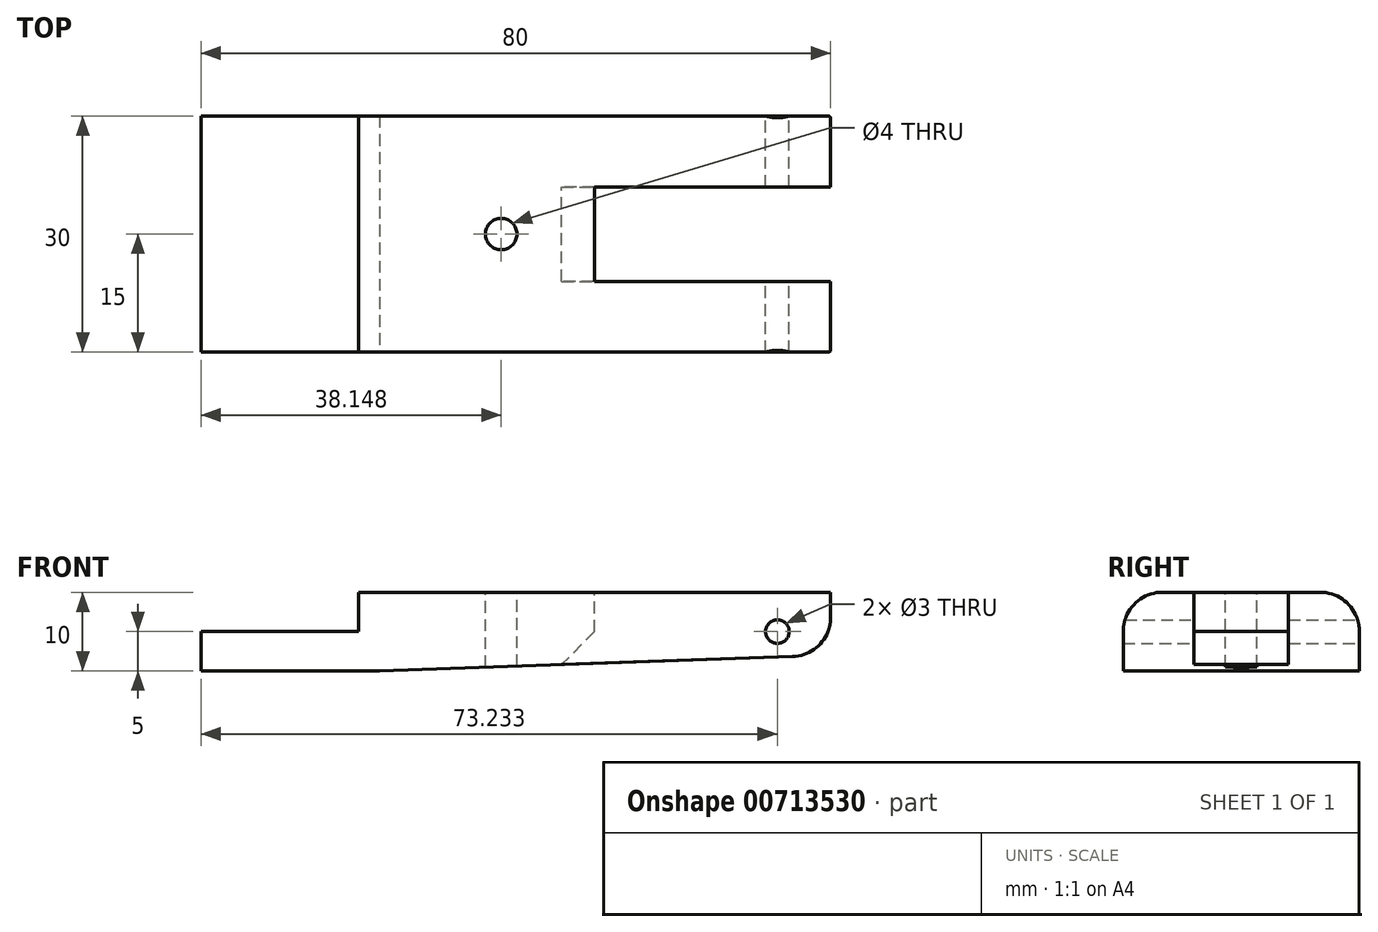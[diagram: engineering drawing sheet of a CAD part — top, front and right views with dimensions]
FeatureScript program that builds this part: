
annotation { "Feature Type Name" : "Feature", "Feature Type Description" : "" }
export const myFeature = defineFeature(function(context is Context, id is Id, definition is map)
    precondition{}
    {
        {
            var Q0;
            Q0=qCreatedBy(makeId("Front.planeOp"),FACE);
            var sketch = newSketch(context, id + "F0", { "sketchPlane" : qUnion([Q0])});
            skLineSegment(sketch, "E0.bottom", {"start": v(0, 0) * mm, "end": v(-80, 0) * mm});
            skLineSegment(sketch, "E0.top", {"start": v(0, 10) * mm, "end": v(-80, 10) * mm});
            skLineSegment(sketch, "E0.left", {"start": v(0, 0) * mm, "end": v(0, 10) * mm});
            skLineSegment(sketch, "E0.right", {"start": v(-80, 0) * mm, "end": v(-80, 10) * mm});
            skCircle(sketch, "E1", {"center": v(-6.77, 5) * mm, "radius": 1.5 * mm});
            skPoint(sketch, "E1.centerSnap0", {"position": v(0, 5) * mm});
            skSolve(sketch);
        }
        {
            var Q0;
            Q0=makeQuery(id+"F0.imprint","IMPRINT",FACE,{"disambiguationData":[TD([[makeQuery(id+"F0.imprint","IMPRINT",EDGE,{"derivedFrom":sQuery(id+"F0.wireOp",EDGE,"E0.bottom")}),-1.0]])]});
            extrude(context, id + "F1", {"entities" : qUnion([Q0]), "depth" : 30 * mm, "offsetDistance" : 25 * mm});
        }
        {
            var Q0;
            Q0=makeQuery(id+"F1.opExtrude","SWEPT_FACE",FACE,{"disambiguationData":[OSD([sQuery(id+"F0.wireOp",EDGE,"E0.top")])]});
            var sketch = newSketch(context, id + "F2", { "sketchPlane" : qUnion([Q0])});
            skLineSegment(sketch, "E2.bottom", {"start": v(0, -9) * mm, "end": v(-30, -9) * mm});
            skLineSegment(sketch, "E2.top", {"start": v(0, -21) * mm, "end": v(-30, -21) * mm});
            skLineSegment(sketch, "E2.left", {"start": v(0, -9) * mm, "end": v(0, -21) * mm});
            skLineSegment(sketch, "E2.right", {"start": v(-30, -9) * mm, "end": v(-30, -21) * mm});
            skPoint(sketch, "E2.middle", {"position": v(-15, -15) * mm});
            skPoint(sketch, "E2.middle.positionSnap0", {"position": v(0, -15) * mm});
            skPoint(sketch, "E2.centerSnap0", {"position": v(0, -15) * mm});
            skSolve(sketch);
        }
        {
            var Q0;
            Q0=makeQuery(id+"F2.imprint","IMPRINT",FACE,{"disambiguationData":[TD([[makeQuery(id+"F2.imprint","IMPRINT",EDGE,{"derivedFrom":sQuery(id+"F2.wireOp",EDGE,"E2.bottom")}),1.0]])]});
            extrude(context, id + "F3", {"entities" : qUnion([Q0]), "operationType" : NewBodyOperationType.REMOVE, "oppositeDirection" : true, "depth" : 25 * mm, "offsetDistance" : 25 * mm});
        }
        {
            var Q0;
            {var subQ0=sQuery(id+"F0.wireOp",EDGE,"E0.left");var subQ4=sQuery(id+"F0.wireOp",EDGE,"E0.top");Q0=makeQuery(id+"FIzBjTdNoyrMJFe_1.boolean.opBoolean","SPLIT",FACE,{"disambiguationData":[TD([makeQuery(id+"F1.opExtrude","SWEPT_FACE",FACE,{"disambiguationData":[OSD([subQ0])]})])],"derivedFrom":makeQuery(id+"F1.opExtrude","SWEPT_FACE",FACE,{"disambiguationData":[OSD([subQ4])]})});}
            var sketch = newSketch(context, id + "F4", { "sketchPlane" : qUnion([Q0])});
            skSolve(sketch);
        }
        {
            var Q0;
            {var subQ0=sQuery(id+"F0.wireOp",EDGE,"E0.left");var subQ4=sQuery(id+"F0.wireOp",EDGE,"E0.top");Q0=makeQuery(id+"FIzBjTdNoyrMJFe_1.boolean.opBoolean","SPLIT",FACE,{"disambiguationData":[TD([makeQuery(id+"F1.opExtrude","SWEPT_FACE",FACE,{"disambiguationData":[OSD([subQ0])]})])],"derivedFrom":makeQuery(id+"F1.opExtrude","SWEPT_FACE",FACE,{"disambiguationData":[OSD([subQ4])]})});}
            var sketch = newSketch(context, id + "F5", { "sketchPlane" : qUnion([Q0])});
            skCircle(sketch, "E3", {"center": v(-41.85, -15) * mm, "radius": 2 * mm});
            skPoint(sketch, "E3.centerSnap0", {"position": v(-42.07, -15) * mm});
            skPoint(sketch, "E4", {"position": v(-30, -15) * mm});
            skSolve(sketch);
        }
        {
            var Q0;
            Q0=makeQuery(id+"F5.imprint","IMPRINT",FACE,{"disambiguationData":[TD([[makeQuery(id+"F5.imprint","IMPRINT",EDGE,{"derivedFrom":sQuery(id+"F5.wireOp",EDGE,"E3")}),1.0]])]});
            extrude(context, id + "F6", {"entities" : qUnion([Q0]), "operationType" : NewBodyOperationType.REMOVE, "oppositeDirection" : true, "depth" : 25 * mm, "offsetDistance" : 25 * mm});
        }
        {
            var Q0;
            Q0=makeQuery(id+"F3.boolean.opBoolean","INTERSECT",EDGE,{"derivedFrom":[makeQuery(id+"F1.opExtrude","SWEPT_FACE",FACE,{"disambiguationData":[OSD([sQuery(id+"F0.wireOp",EDGE,"E0.bottom")])]}),makeQuery(id+"F3.opExtrude","SWEPT_FACE",FACE,{"disambiguationData":[OSD([sQuery(id+"F2.wireOp",EDGE,"E2.right")])]})]});
            chamfer(context, id + "F7", {"entities" : qUnion([Q0]), "width" : 5 * mm, "tangentPropagation" : true});
        }
        {
            var Q0;
            {var subQ1=sQuery(id+"F0.wireOp",EDGE,"E0.top");Q0=makeQuery(id+"F4.imprint","IMPRINT",FACE,{"disambiguationData":[TD([[makeQuery(id+"F4.imprint","IMPRINT",EDGE,{"derivedFrom":makeQuery(id+"F1.opExtrude","CAP_EDGE",EDGE,{"disambiguationData":[OSD([subQ1])],"isStart":true})}),1.0]])]});}
            var sketch = newSketch(context, id + "F8", { "sketchPlane" : qUnion([Q0])});
            skLineSegment(sketch, "E5.bottom", {"start": v(-80, 0) * mm, "end": v(-60, 0) * mm});
            skLineSegment(sketch, "E5.top", {"start": v(-80, -30) * mm, "end": v(-60, -30) * mm});
            skLineSegment(sketch, "E5.left", {"start": v(-80, 0) * mm, "end": v(-80, -30) * mm});
            skLineSegment(sketch, "E5.right", {"start": v(-60, 0) * mm, "end": v(-60, -30) * mm});
            skSolve(sketch);
        }
        {
            var Q0;
            Q0=makeQuery(id+"F8.imprint","IMPRINT",FACE,{"disambiguationData":[TD([[makeQuery(id+"F8.imprint","IMPRINT",EDGE,{"derivedFrom":sQuery(id+"F8.wireOp",EDGE,"E5.bottom")}),1.0]])]});
            extrude(context, id + "F9", {"entities" : qUnion([Q0]), "operationType" : NewBodyOperationType.REMOVE, "oppositeDirection" : true, "depth" : 5 * mm, "offsetDistance" : 25 * mm});
        }
        {
            var Q0;
            Q0=makeQuery(id+"F9.boolean.opBoolean","COPY",EDGE,{"derivedFrom":makeQuery(id+"F9.opExtrude","CAP_EDGE",EDGE,{"disambiguationData":[OSD([sQuery(id+"F8.wireOp",EDGE,"E5.left")])],"isStart":false})});
            var Q1;
            Q1=makeQuery(id+"F9.boolean.opBoolean","COPY",EDGE,{"derivedFrom":makeQuery(id+"F9.opExtrude","CAP_EDGE",EDGE,{"disambiguationData":[OSD([sQuery(id+"F8.wireOp",EDGE,"E5.top")])],"isStart":false})});
            var Q2;
            Q2=makeQuery(id+"F9.boolean.opBoolean","COPY",EDGE,{"derivedFrom":makeQuery(id+"F9.opExtrude","CAP_EDGE",EDGE,{"disambiguationData":[OSD([sQuery(id+"F8.wireOp",EDGE,"E5.bottom")])],"isStart":false})});
            var Q3;
            Q3=makeQuery(id+"F1.opExtrude","CAP_EDGE",EDGE,{"disambiguationData":[OSD([sQuery(id+"F0.wireOp",EDGE,"E0.top")])],"isStart":false});
            var Q4;
            Q4=makeQuery(id+"F1.opExtrude","CAP_EDGE",EDGE,{"disambiguationData":[OSD([sQuery(id+"F0.wireOp",EDGE,"E0.top")])],"isStart":true});
            var Q5;
            Q5=makeQuery(id+"F3.boolean.opBoolean","COPY",EDGE,{"derivedFrom":makeQuery(id+"F3.opExtrude","CAP_EDGE",EDGE,{"disambiguationData":[OSD([sQuery(id+"F2.wireOp",EDGE,"E2.bottom")])],"isStart":true})});
            var Q6;
            Q6=makeQuery(id+"F3.boolean.opBoolean","COPY",EDGE,{"derivedFrom":makeQuery(id+"F3.opExtrude","CAP_EDGE",EDGE,{"disambiguationData":[OSD([sQuery(id+"F2.wireOp",EDGE,"E2.top")])],"isStart":true})});
            var Q7;
            Q7=makeQuery(id+"F3.boolean.opBoolean","COPY",EDGE,{"derivedFrom":makeQuery(id+"F3.opExtrude","CAP_EDGE",EDGE,{"disambiguationData":[OSD([sQuery(id+"F2.wireOp",EDGE,"E2.right")])],"isStart":true})});
            fillet(context, id + "F10", {"entities" : qUnion([Q0, Q1, Q2, Q3, Q4, Q5, Q6, Q7]), "radius" : 5 * mm, "tangentPropagation" : true, "allowEdgeOverflow" : false});
        }
        {
            var Q0;
            {var subQ0=sQuery(id+"F0.wireOp",EDGE,"E0.bottom");var subQ1=sQuery(id+"F0.wireOp",EDGE,"E0.left");Q0=makeQuery(id+"F3.boolean.opBoolean","SPLIT",EDGE,{"disambiguationData":[TD([makeQuery(id+"F3.opExtrude","SWEPT_FACE",FACE,{"disambiguationData":[OSD([sQuery(id+"F2.wireOp",EDGE,"E2.bottom")])]})])],"derivedFrom":makeQuery(id+"F1.opExtrude","SWEPT_EDGE",EDGE,{"disambiguationData":[OSD([subQ0,subQ1])]})});}
            var Q1;
            {var subQ0=sQuery(id+"F0.wireOp",EDGE,"E0.bottom");var subQ1=sQuery(id+"F0.wireOp",EDGE,"E0.left");Q1=makeQuery(id+"F3.boolean.opBoolean","SPLIT",EDGE,{"disambiguationData":[TD([makeQuery(id+"F3.opExtrude","SWEPT_FACE",FACE,{"disambiguationData":[OSD([sQuery(id+"F2.wireOp",EDGE,"E2.top")])]})])],"derivedFrom":makeQuery(id+"F1.opExtrude","SWEPT_EDGE",EDGE,{"disambiguationData":[OSD([subQ0,subQ1])]})});}
            chamfer(context, id + "F11", {"entities" : qUnion([Q0, Q1]), "chamferType" : ChamferType.OFFSET_ANGLE, "width" : 2 * mm, "oppositeDirection" : false, "angle" : 88 * degree, "tangentPropagation" : true});
        }
        {
            var Q0;
            {var subQ0=sQuery(id+"F0.wireOp",EDGE,"E0.bottom");var subQ2=sQuery(id+"F0.wireOp",EDGE,"E0.left");var subQ5=makeQuery(id+"F3.opExtrude","SWEPT_FACE",FACE,{"disambiguationData":[OSD([sQuery(id+"F2.wireOp",EDGE,"E2.bottom")])]});var subQ6=makeQuery(id+"F1.opExtrude","SWEPT_FACE",FACE,{"disambiguationData":[OSD([subQ2])]});Q0=makeQuery(id+"F11.opChamfer","BLEND_EDGE",EDGE,{"blendedFrom":[makeQuery(id+"F3.boolean.opBoolean","SPLIT",EDGE,{"disambiguationData":[TD([subQ5])],"derivedFrom":makeQuery(id+"F1.opExtrude","SWEPT_EDGE",EDGE,{"disambiguationData":[OSD([subQ0,subQ2])]})}),makeQuery(id+"F3.boolean.opBoolean","SPLIT",FACE,{"disambiguationData":[TD([subQ5])],"derivedFrom":subQ6})],"blendedInto":[makeQuery(id+"F3.boolean.opBoolean","SPLIT",FACE,{"disambiguationData":[TD([subQ5])],"derivedFrom":subQ6})]});}
            var Q1;
            {var subQ0=sQuery(id+"F0.wireOp",EDGE,"E0.bottom");var subQ4=sQuery(id+"F0.wireOp",EDGE,"E0.left");var subQ6=makeQuery(id+"F1.opExtrude","SWEPT_FACE",FACE,{"disambiguationData":[OSD([subQ4])]});Q1=makeQuery(id+"F11.opChamfer","BLEND_EDGE",EDGE,{"blendedFrom":[makeQuery(id+"F3.boolean.opBoolean","SPLIT",EDGE,{"disambiguationData":[TD([makeQuery(id+"F3.opExtrude","SWEPT_FACE",FACE,{"disambiguationData":[OSD([sQuery(id+"F2.wireOp",EDGE,"E2.bottom")])]})])],"derivedFrom":makeQuery(id+"F1.opExtrude","SWEPT_EDGE",EDGE,{"disambiguationData":[OSD([subQ0,subQ4])]})}),makeQuery(id+"F3.boolean.opBoolean","SPLIT",FACE,{"disambiguationData":[TD([makeQuery(id+"F3.opExtrude","SWEPT_FACE",FACE,{"disambiguationData":[OSD([sQuery(id+"F2.wireOp",EDGE,"E2.top")])]})])],"derivedFrom":subQ6})],"blendedInto":[makeQuery(id+"F3.boolean.opBoolean","SPLIT",FACE,{"disambiguationData":[TD([makeQuery(id+"F3.opExtrude","SWEPT_FACE",FACE,{"disambiguationData":[OSD([sQuery(id+"F2.wireOp",EDGE,"E2.top")])]})])],"derivedFrom":subQ6})]});}
            fillet(context, id + "F12", {"entities" : qUnion([Q0, Q1]), "radius" : 5 * mm, "tangentPropagation" : true, "allowEdgeOverflow" : false});
        }
    });
